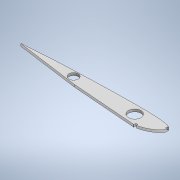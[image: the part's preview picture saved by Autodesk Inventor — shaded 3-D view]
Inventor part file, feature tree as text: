
AUTODESK INVENTOR PART (.ipt)
format: ipt  version: 2022 (Build 260153000, 153)  size: 175,104 bytes
history: native  units: mm
features: extrude x1, sketch x1
ambient origin geometry x8: Origin, YZ Plane, XZ Plane, XY Plane, X Axis, Y Axis, Z Axis, Center Point
bodies: Body1 (feature_tree)
feature tree (2):
  extrude  "Extrusion4"  Depth=160.0mm
  sketch  "Sketch1"  dims[d5=160.0mm d8=160.0mm d17=5.0mm d18=5.0mm d25=6.0mm d26=5.0mm d27=5.0mm d31=34.456mm d36=5.0mm d37=5.0mm d41=23.0mm d50=368.759386mm d60=8.0mm d62=31.0mm d63=6.0mm d64=0.0mm]
